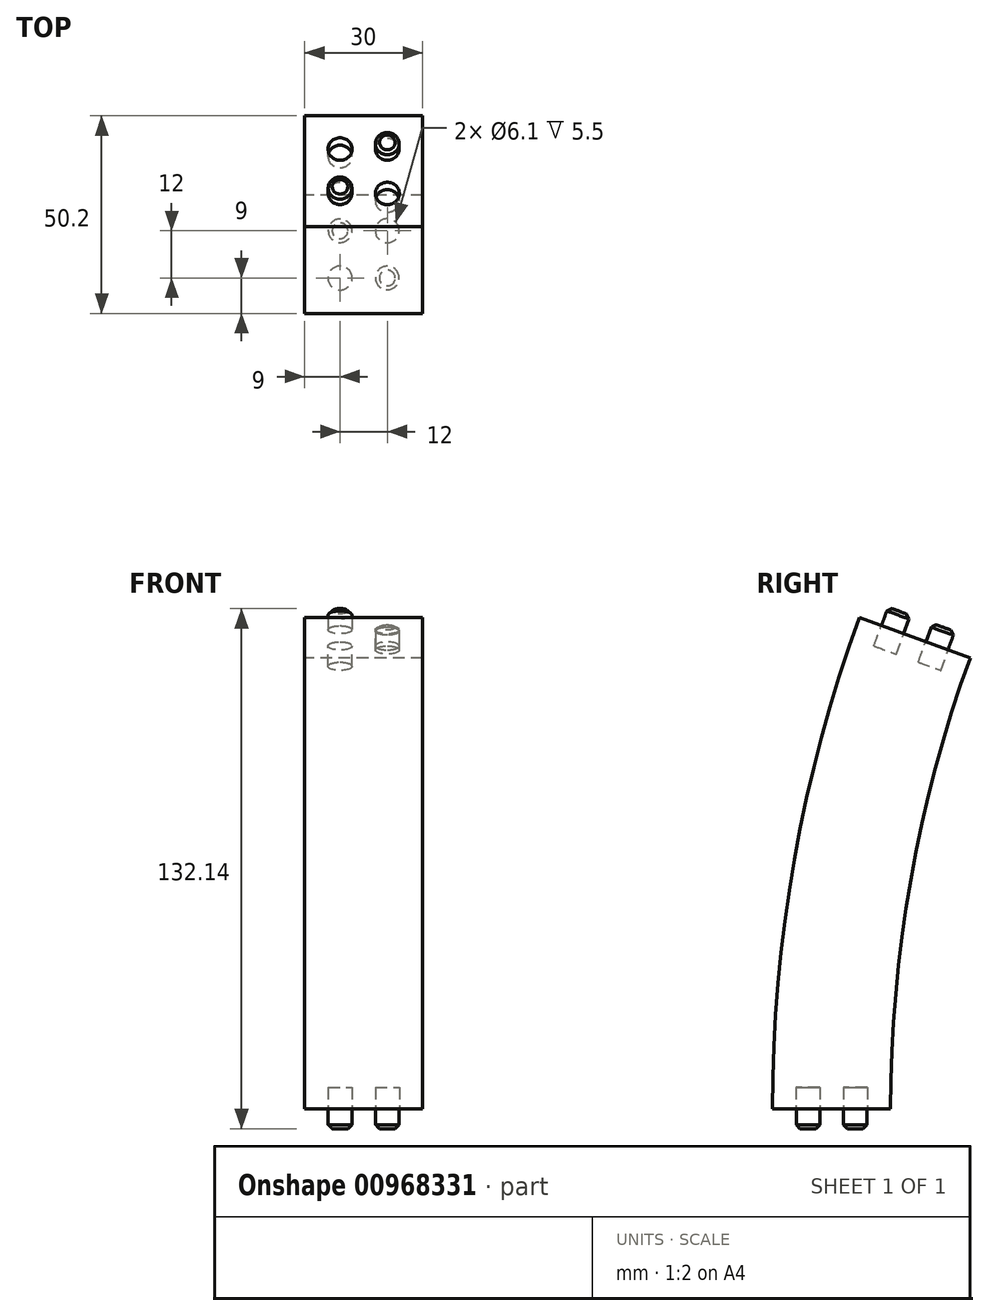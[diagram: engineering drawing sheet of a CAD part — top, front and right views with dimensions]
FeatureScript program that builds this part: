
annotation { "Feature Type Name" : "Feature", "Feature Type Description" : "" }
export const myFeature = defineFeature(function(context is Context, id is Id, definition is map)
    precondition{}
    {
        {
            var Q0;
            Q0=qCreatedBy(makeId("Right.planeOp"),FACE);
            var sketch = newSketch(context, id + "F0", { "sketchPlane" : qUnion([Q0])});
            skLineSegment(sketch, "E0", {"start": v(-15, 0) * mm, "end": v(15, 0) * mm});
            skLineSegment(sketch, "E1", {"start": v(0, 0) * mm, "end": v(350, 0) * mm, "construction": true});
            skLineSegment(sketch, "E2", {"start": v(350, 0) * mm, "end": v(-25.88, 136.8) * mm, "construction": true});
            skArc(sketch, "E3", {"start": v(15, 0) * mm, "mid": v(20.09, 58.17) * mm, "end": v(35.2, 114.58) * mm});
            skArc(sketch, "E4", {"start": v(-15, 0) * mm, "mid": v(-9.45, 63.38) * mm, "end": v(7.01, 124.84) * mm});
            skLineSegment(sketch, "E5", {"start": v(35.2, 114.58) * mm, "end": v(7.01, 124.84) * mm});
            skSolve(sketch);
        }
        {
            var Q0;
            Q0 = qSketchRegion(id + "F0", true);
            extrude(context, id + "F1", {"entities" : qUnion([Q0]), "depth" : 30 * mm, "offsetDistance" : 25 * mm});
        }
        {
            var Q0;
            Q0=makeQuery(id+"F1.opExtrude","SWEPT_FACE",FACE,{"disambiguationData":[OSD([sQuery(id+"F0.wireOp",EDGE,"E5")])]});
            var sketch = newSketch(context, id + "F2", { "sketchPlane" : qUnion([Q0])});
            skCircle(sketch, "E6", {"center": v(9, -27.1) * mm, "radius": 3 * mm});
            skCircle(sketch, "E7", {"center": v(21, -15.1) * mm, "radius": 3 * mm});
            skSolve(sketch);
        }
        {
            var Q0;
            Q0 = qSketchRegion(id + "F2", true);
            extrude(context, id + "F3", {"entities" : qUnion([Q0]), "operationType" : NewBodyOperationType.ADD, "depth" : 5 * mm, "offsetDistance" : 25 * mm});
        }
        {
            var Q0;
            Q0=makeQuery(id+"F3.opExtrude","CAP_EDGE",EDGE,{"disambiguationData":[OSD([sQuery(id+"F2.wireOp",EDGE,"E6")])],"isStart":false});
            var Q1;
            Q1=makeQuery(id+"F3.opExtrude","CAP_EDGE",EDGE,{"disambiguationData":[OSD([sQuery(id+"F2.wireOp",EDGE,"E7")])],"isStart":false});
            chamfer(context, id + "F4", {"entities" : qUnion([Q0, Q1]), "width" : 1 * mm, "tangentPropagation" : true});
        }
        {
            var Q0;
            Q0=makeQuery(id+"F1.opExtrude","SWEPT_FACE",FACE,{"disambiguationData":[OSD([sQuery(id+"F0.wireOp",EDGE,"E0")])]});
            var sketch = newSketch(context, id + "F5", { "sketchPlane" : qUnion([Q0])});
            skCircle(sketch, "E8", {"center": v(9, -6) * mm, "radius": 3 * mm});
            skCircle(sketch, "E9", {"center": v(21, 6) * mm, "radius": 3 * mm});
            skSolve(sketch);
        }
        {
            var Q0;
            Q0 = qSketchRegion(id + "F5", true);
            extrude(context, id + "F6", {"entities" : qUnion([Q0]), "operationType" : NewBodyOperationType.ADD, "depth" : 5 * mm, "offsetDistance" : 25 * mm});
        }
        {
            var Q0;
            Q0=makeQuery(id+"F6.opExtrude","CAP_EDGE",EDGE,{"disambiguationData":[OSD([sQuery(id+"F5.wireOp",EDGE,"E8")])],"isStart":false});
            var Q1;
            Q1=makeQuery(id+"F6.opExtrude","CAP_EDGE",EDGE,{"disambiguationData":[OSD([sQuery(id+"F5.wireOp",EDGE,"E9")])],"isStart":false});
            chamfer(context, id + "F7", {"entities" : qUnion([Q0, Q1]), "width" : 1 * mm, "tangentPropagation" : true});
        }
        {
            var Q0;
            Q0=makeQuery(id+"F1.opExtrude","SWEPT_FACE",FACE,{"disambiguationData":[OSD([sQuery(id+"F0.wireOp",EDGE,"E5")])]});
            var sketch = newSketch(context, id + "F8", { "sketchPlane" : qUnion([Q0])});
            skCircle(sketch, "E10", {"center": v(9, -15.1) * mm, "radius": 3.05 * mm});
            skCircle(sketch, "E11", {"center": v(21, -27.1) * mm, "radius": 3.05 * mm});
            skSolve(sketch);
        }
        {
            var Q0;
            Q0 = qSketchRegion(id + "F8", true);
            extrude(context, id + "F9", {"entities" : qUnion([Q0]), "operationType" : NewBodyOperationType.REMOVE, "oppositeDirection" : true, "depth" : 5.5 * mm, "offsetDistance" : 25 * mm});
        }
        {
            var Q0;
            Q0=makeQuery(id+"F1.opExtrude","SWEPT_FACE",FACE,{"disambiguationData":[OSD([sQuery(id+"F0.wireOp",EDGE,"E0")])]});
            var sketch = newSketch(context, id + "F10", { "sketchPlane" : qUnion([Q0])});
            skCircle(sketch, "E12", {"center": v(9, 6) * mm, "radius": 3.05 * mm});
            skCircle(sketch, "E13", {"center": v(21, -6) * mm, "radius": 3.05 * mm});
            skSolve(sketch);
        }
        {
            var Q0;
            Q0 = qSketchRegion(id + "F10", true);
            extrude(context, id + "F11", {"entities" : qUnion([Q0]), "operationType" : NewBodyOperationType.REMOVE, "oppositeDirection" : true, "depth" : 5.5 * mm, "offsetDistance" : 25 * mm});
        }
    });
